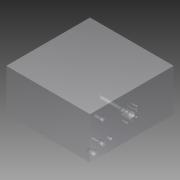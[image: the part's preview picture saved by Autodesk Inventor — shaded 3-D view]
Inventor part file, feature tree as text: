
AUTODESK INVENTOR PART (.ipt)
format: ipt  version: 2014 (Build 180170000, 170)  size: 479,744 bytes
history: native  units: mm
features: extrude x48, other x48, sketch x48
ambient origin geometry x8: Origin, YZ Plane, XZ Plane, XY Plane, X Axis, Y Axis, Z Axis, Center Point
bodies: 实体1 (feature_tree)
feature tree (144):
  extrude  "拉伸1"  Depth=30.0mm
  other  "UCS1"
  other  "UCS2"
  other  "UCS3"
  other  "UCS4"
  other  "UCS5"
  other  "UCS6"
  extrude  "拉伸3"  Depth=60.0mm
  extrude  "拉伸5"  Depth=2.0mm
  extrude  "拉伸6"  Depth=2.4mm
  extrude  "拉伸7"  Depth=14.5mm TaperAngle=0.0deg
  extrude  "拉伸8"  Depth=16.5mm TaperAngle=0.0deg
  extrude  "拉伸9"  Depth=11.0mm
  extrude  "拉伸10"  Depth=50.8mm
  extrude  "拉伸11"  Depth=150.0mm
  extrude  "拉伸12"  Depth=1.5mm TaperAngle=0.0deg
  extrude  "拉伸13"  Depth=12.5mm TaperAngle=0.0deg
  extrude  "拉伸14"  Depth=16.0mm TaperAngle=0.0deg
  extrude  "拉伸15"  Depth=14.0mm
  extrude  "拉伸16"  Depth=38.1mm
  extrude  "拉伸17"  Depth=14.0mm
  extrude  "拉伸18"  Depth=14.5mm TaperAngle=0.0deg
  extrude  "拉伸20"  Depth=12.7mm
  extrude  "拉伸21"  Depth=20.0mm
  extrude  "拉伸22"  Depth=100.0mm
  extrude  "拉伸23"  Depth=200.0mm
  extrude  "拉伸24"  Depth=10.0mm
  extrude  "拉伸25"  Depth=43.0mm TaperAngle=0.0deg
  extrude  "拉伸26"  Depth=13.0mm
  extrude  "拉伸28"  Depth=56.0mm TaperAngle=0.0deg
  extrude  "拉伸29"  Depth=16.0mm TaperAngle=0.0deg
  extrude  "拉伸30"  Depth=6.75mm
  extrude  "拉伸31"  Depth=23.0mm
  extrude  "拉伸32"  Depth=23.0mm
  extrude  "拉伸33"  Depth=23.0mm
  extrude  "拉伸34"  Depth=23.0mm
  extrude  "拉伸35"  Depth=24.0mm
  extrude  "拉伸36"  Depth=24.0mm
  extrude  "拉伸37"  Depth=8.0mm
  extrude  "拉伸38"  Depth=4.0mm
  extrude  "拉伸39"  TaperAngle=0.0deg  [1 undecoded]
  extrude  "拉伸40"  Depth=25.0mm
  extrude  "拉伸41"  Depth=25.4mm TaperAngle=0.0deg
  extrude  "拉伸42"  Depth=25.4mm
  extrude  "拉伸43"  Depth=4.0mm
  extrude  "拉伸44"  TaperAngle=0.0deg  [1 undecoded]
  extrude  "拉伸45"  TaperAngle=0.0deg  [1 undecoded]
  extrude  "拉伸46"  Depth=0.79mm
  extrude  "拉伸47"  Depth=0.79mm
  extrude  "拉伸48"  Depth=4.0mm
  extrude  "拉伸49"  Depth=0.79mm
  extrude  "拉伸50"  Depth=0.79mm
  extrude  "拉伸51"  Depth=8.0mm TaperAngle=0.0deg
  extrude  "拉伸53"  Depth=8.0mm
  sketch  "草图1"  dims[d0=200.0mm d1=0.0mm]
  sketch  "草图2"  dims[d2=0.0mm d3=0.0mm d4=0.0mm d5=0.0mm d6=0.0mm d7=0.0mm]
  sketch  "草图4"  dims[d8=0.0mm d9=0.0mm d10=0.0mm d11=0.0mm d12=0.0mm d13=0.0mm]
  sketch  "草图5"  dims[d14=0.0mm d15=0.0mm d16=0.0mm d17=0.0mm d18=0.0mm d19=0.0mm]
  sketch  "草图6"  dims[d20=0.0mm d21=0.0mm d22=0.0mm d23=0.0mm d24=0.0mm d25=0.0mm]
  sketch  "草图8"  dims[d26=0.0mm d27=0.0mm d28=0.0mm d29=0.0mm d30=0.0mm d31=0.0mm]
  sketch  "草图9"  dims[d32=0.0mm d33=0.0mm d34=0.0mm d35=0.0mm d36=0.0mm d37=0.0mm d38=30.0mm]
  sketch  "草图10"  dims[d39=50.0mm d40=60.0mm]
  sketch  "草图11"  dims[d43=2.0mm d44=0.0mm d47=19.8mm]
  sketch  "草图15"  dims[d48=2.4mm d49=-2.617994mm d50=2.4mm d51=-7.853982mm]
  sketch  "草图16"  dims[d52=18.0mm d53=14.5mm d54=0.0mm]
  sketch  "草图17"  dims[d55=16.5mm d56=17.0mm d57=0.0mm]
  sketch  "草图18"  dims[d58=17.0mm d59=-10.471976mm d60=11.0mm]
  sketch  "草图19"  dims[d61=50.8mm d62=0.0mm d63=50.8mm d64=-10.297443mm]
  sketch  "草图20"  dims[d74=60.0mm d75=150.0mm]
  sketch  "草图21"  dims[d76=24.5mm d77=1.5mm d78=0.0mm]
  sketch  "草图23"  dims[d79=16.7mm d80=12.5mm d81=0.0mm]
  sketch  "草图24"  dims[d82=15.25mm d83=16.0mm d84=0.0mm]
  sketch  "草图25"  dims[d85=16.0mm d86=-10.297443mm d87=14.0mm]
  sketch  "草图27"  dims[d88=38.1mm d89=0.0mm d90=38.1mm d91=-10.297443mm]
  sketch  "草图28"  dims[d92=14.0mm d93=50.0mm]
  sketch  "草图29"  dims[d94=100.0mm d95=14.5mm d96=0.0mm]
  sketch  "草图31"  dims[d100=20.0mm d101=-10.471976mm d102=12.7mm]
  sketch  "草图32"  dims[d103=20.0mm d104=0.0mm d105=20.0mm d106=-10.297443mm]
  sketch  "草图33"  dims[d110=33.7mm d111=100.0mm]
  sketch  "草图34"  dims[d112=200.0mm d113=65.0mm]
  sketch  "草图35"  dims[d114=65.0mm d115=10.0mm d116=-2.617994mm]
  sketch  "草图36"  dims[d117=32.0mm d118=43.0mm d119=0.0mm]
  sketch  "草图37"  dims[d120=26.07mm d121=13.0mm d122=-2.617994mm]
  sketch  "草图38"  dims[d124=25.0mm d125=56.0mm d126=0.0mm]
  sketch  "草图39"  dims[d127=16.0mm d130=152.4mm d131=0.0mm]
  sketch  "草图40"  dims[d132=152.4mm d133=-10.297443mm d134=6.75mm]
  sketch  "草图41"  dims[d135=23.0mm d136=23.0mm]
  sketch  "草图42"  dims[d137=23.0mm d138=23.0mm]
  sketch  "草图43"  dims[d139=23.0mm d140=23.0mm]
  sketch  "草图44"  dims[d141=23.0mm d142=23.0mm]
  sketch  "草图45"  dims[d143=24.0mm d144=0.0mm d145=24.0mm d146=-10.297443mm]
  sketch  "草图46"  dims[d147=24.0mm d148=-10.297443mm d149=24.0mm d150=-10.297443mm]
  sketch  "草图47"  dims[d151=24.0mm d152=-10.297443mm d153=8.0mm]
  sketch  "草图54"  dims[d154=16.0mm d155=0.0mm d156=4.0mm]
  sketch  "草图55"  dims[d157=4.0mm d160=0.0mm]
  sketch  "草图56"  dims[d161=0.0mm d162=25.0mm]
  sketch  "草图57"  dims[d163=25.000195mm d164=25.4mm d165=0.0mm]
  sketch  "草图58"  dims[d166=25.4mm d167=-10.297443mm d168=25.4mm d169=-10.297443mm]
  sketch  "草图59"  dims[d170=4.0mm d171=4.0mm]
  sketch  "草图60"  dims[d172=25.0mm d173=0.0mm]
  sketch  "草图61"  dims[d174=25.0mm d175=0.0mm]
  sketch  "草图63"  dims[d176=25.4mm d177=0.0mm d178=25.4mm d179=-10.297443mm d180=25.4mm d181=-10.297443mm d182=4.0mm d183=23.0mm d184=10.5mm d185=8.0mm d186=0.0mm d187=8.0mm d188=-10.297443mm d267=30.0mm d268=20.0mm d269=34.14mm d270=0.79mm d271=0.0mm d272=23.93mm d273=2.54mm d274=-2.617994mm d275=2.54mm d276=-7.853982mm d277=22.22mm d278=16.66mm d279=0.0mm d280=16.66mm d281=-10.471976mm d282=20.27mm d283=19.84mm d284=0.0mm d285=19.84mm d286=-10.471976mm d287=19.0mm d288=25.4mm d289=0.0mm d292=25.4mm d293=-10.471976mm]
  other  "UCS1: YZ 平面"
  other  "UCS1: XZ 平面"
  other  "UCS1: XY 平面"
  other  "UCS1: X 轴"
  other  "UCS1: Y 轴"
  other  "UCS1: Z 轴"
  other  "UCS1: 原点"
  other  "UCS2: YZ 平面"
  other  "UCS2: XZ 平面"
  other  "UCS2: XY 平面"
  other  "UCS2: X 轴"
  other  "UCS2: Y 轴"
  other  "UCS2: Z 轴"
  other  "UCS2: 原点"
  other  "UCS3: YZ 平面"
  other  "UCS3: XZ 平面"
  other  "UCS3: XY 平面"
  other  "UCS3: X 轴"
  other  "UCS3: Y 轴"
  other  "UCS3: Z 轴"
  other  "UCS3: 原点"
  other  "UCS4: YZ 平面"
  other  "UCS4: XZ 平面"
  other  "UCS4: XY 平面"
  other  "UCS4: X 轴"
  other  "UCS4: Y 轴"
  other  "UCS4: Z 轴"
  other  "UCS4: 原点"
  other  "UCS5: YZ 平面"
  other  "UCS5: XZ 平面"
  other  "UCS5: XY 平面"
  other  "UCS5: X 轴"
  other  "UCS5: Y 轴"
  other  "UCS5: Z 轴"
  other  "UCS5: 原点"
  other  "UCS6: YZ 平面"
  other  "UCS6: XZ 平面"
  other  "UCS6: XY 平面"
  other  "UCS6: X 轴"
  other  "UCS6: Y 轴"
  other  "UCS6: Z 轴"
  other  "UCS6: 原点"
note: 3 required parameter values undecoded (feature->parameter linkage not recoverable at this tier; creation-order binding heuristic only, values carry confidence <= 0.55)
